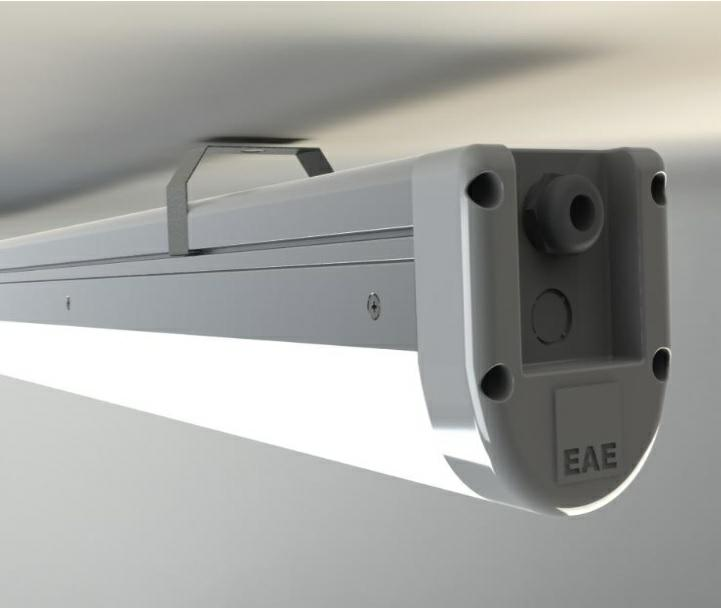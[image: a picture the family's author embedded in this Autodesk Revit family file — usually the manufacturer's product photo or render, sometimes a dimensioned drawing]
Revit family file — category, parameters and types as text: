
# Revit family: LINA
name_source: partatom
category: Lighting Fixtures
revit_build: Autodesk Revit 2016 (Build: 20150506_1715(x64)
units: mm (PartAtom-declared; Revit-internal decimal feet)

## family parameters
Cut with Voids When Loaded = No
Host = Face
Light Source = Yes
OmniClass Number = 23.80.70.11.14.17
OmniClass Title = Direct/Indirect
Part Type = Normal
Room Calculation Point = No
Round Connector Dimension = Use Diameter
Shared = No

## types (42) — shared parameters
Apparent Load = 0 VA
Assembly Code = D5020200
Ağırlık = 0.0 kg
Color Filter = 16777215
Description = SURFACE MOUNTED
Dimming Lamp Color Temperature Shift = <None>
EAE_CYi_Alum_Kasa = EAE_CYi_Alum_Kasa
EAE_CYi_Temperli Cam = EAE_CYi_Temperli Cam
Giriş Gerilimi = 220 V
IP Koruma Sınıfı = IP 65
Keynote = Catalog Number
Lamp = DO NOT USE
Lookup Table = EAE_Lookup_Annotation
Lookup Table Name = LINA
Manufacturer = EAE
Model = LINA
Photometric Web File = 1x4 2Lamp.ies
Renksel Geri Verim = CRI 80
Tilt Angle = 90.00°
Type Comments = PLEASE CONSULT EAE FOR CODE DESCRIPTION
Type Image = LINA ETANJ.jpg
URL = http://www.eaeaydinlatma.com
Wattage Comments = DO NOT USE
b = 66 mm  [stored 0.216535 ft]
h = 86 mm  [stored 0.282152 ft]
Çalışma Ortam Sıcaklığı = -25 °C / +40 °C
zero-valued in all types: Default Elevation

## per-type parameters (varying)
| type | Anma Gücü | AnnoText | Catalog Number | Emit from Line Length | Kontrol Sistem Girişi | a |
| LNE 020U 40ED00 2K0 053 | 20 W | 0 | 48407 | 512 mm  [stored 1.67979 ft] | NOT SPECIFIED | 532 mm  [stored 1.74541 ft] |
| LNE 020U 40ED01 2K0 053 | 20 W | 1 | 48408 | 512 mm  [stored 1.67979 ft] | E1h | 532 mm  [stored 1.74541 ft] |
| LNE 020U 40ED03 2K9 053 | 20 W | 3 | 48410 | 512 mm  [stored 1.67979 ft] | DALI | 532 mm  [stored 1.74541 ft] |
| LNE 020U 40ED04 2K0 053 | 20 W | 4 | 48411 | 512 mm  [stored 1.67979 ft] | DALI E1h | 532 mm  [stored 1.74541 ft] |
| LNE 020U 40ED09 2K0 063 | 20 W | 9 | 48413 | 512 mm  [stored 1.67979 ft] | SNS | 532 mm  [stored 1.74541 ft] |
| LNE 020U 40ED10 2K0 063 | 20 W | 10 | 48602 | 512 mm  [stored 1.67979 ft] | SNS E1h | 532 mm  [stored 1.74541 ft] |
| LNE 032U 40ED00 3K3 125 | 32 W | 0 | 43677 | 1230 mm  [stored 4.03543 ft] | NOT SPECIFIED | 1250 mm  [stored 4.10105 ft] |
| LNE 032U 40ED01 3K3 125 | 32 W | 1 | 43678 | 1230 mm  [stored 4.03543 ft] | E1h | 1250 mm  [stored 4.10105 ft] |
| LNE 032U 40ED02 3K3 125 | 32 W | 2 | 43679 | 1230 mm  [stored 4.03543 ft] | E3h | 1250 mm  [stored 4.10105 ft] |
| LNE 032U 40ED03 3K3 125 | 32 W | 3 | 43680 | 1230 mm  [stored 4.03543 ft] | DALI | 1250 mm  [stored 4.10105 ft] |
| LNE 032U 40ED04 3K3 125 | 32 W | 4 | 43681 | 1230 mm  [stored 4.03543 ft] | DALI E1h | 1250 mm  [stored 4.10105 ft] |
| LNE 032U 40ED05 3K3 125 | 32 W | 5 | 43682 | 1230 mm  [stored 4.03543 ft] | DALI E3h | 1250 mm  [stored 4.10105 ft] |
| LNE 032U 40ED09 3K3 135 | 32 W | 9 | 43683 | 1230 mm  [stored 4.03543 ft] | SNS | 1250 mm  [stored 4.10105 ft] |
| LNE 032U 40ED10 3K3 135 | 32 W | 10 | 48617 | 1230 mm  [stored 4.03543 ft] | SNS E1h | 1250 mm  [stored 4.10105 ft] |
| LNE 032U 40ED11 3K3 135 | 32 W | 11 | 48618 | 1230 mm  [stored 4.03543 ft] | SNS E3h | 1250 mm  [stored 4.10105 ft] |
| LNE 040U 40ED00 LLL 149 | 40 W | 0 | 48449 | 1470 mm  [stored 4.82283 ft] | NOT SPECIFIED | 1490 mm  [stored 4.88845 ft] |
| LNE 040U 40ED01 LLL 149 | 40 W | 1 | 48450 | 1470 mm  [stored 4.82283 ft] | E1h | 1490 mm  [stored 4.88845 ft] |
| LNE 040U 40ED02 LLL 149 | 40 W | 2 | 48451 | 1470 mm  [stored 4.82283 ft] | E3h | 1490 mm  [stored 4.88845 ft] |
| LNE 040U 40ED03 LLL 149 | 40 W | 3 | 48452 | 1470 mm  [stored 4.82283 ft] | DALI | 1490 mm  [stored 4.88845 ft] |
| LNE 040U 40ED04 LLL 149 | 40 W | 4 | 48453 | 1470 mm  [stored 4.82283 ft] | DALI E1h | 1490 mm  [stored 4.88845 ft] |
| LNE 040U 40ED05 LLL 149 | 40 W | 5 | 48454 | 1470 mm  [stored 4.82283 ft] | DALI E3h | 1490 mm  [stored 4.88845 ft] |
| LNE 040U 40ED09 LLL 159 | 40 W | 9 | 48455 | 1470 mm  [stored 4.82283 ft] | SNS | 1490 mm  [stored 4.88845 ft] |
| LNE 040U 40ED10 LLL 159 | 40 W | 10 | 48635 | 1470 mm  [stored 4.82283 ft] | SNS E1h | 1490 mm  [stored 4.88845 ft] |
| LNE 040U 40ED11 LLL 159 | 40 W | 11 | 48636 | 1470 mm  [stored 4.82283 ft] | SNS E3h | 1490 mm  [stored 4.88845 ft] |
| LNE 045U 40ED00 4K9 085 | 45 W | 0 | 48470 | 830 mm  [stored 2.7231 ft] | NOT SPECIFIED | 850 mm  [stored 2.78871 ft] |
| LNE 045U 40ED01 4K9 085 | 45 W | 1 | 48471 | 830 mm  [stored 2.7231 ft] | E1h | 850 mm  [stored 2.78871 ft] |
| LNE 045U 40ED02 4K9 085 | 45 W | 2 | 48472 | 830 mm  [stored 2.7231 ft] | E3h | 850 mm  [stored 2.78871 ft] |
| LNE 045U 40ED03 4K9 085 | 45 W | 3 | 48473 | 830 mm  [stored 2.7231 ft] | DALI | 850 mm  [stored 2.78871 ft] |
| LNE 045U 40ED04 4K9 085 | 45 W | 4 | 48474 | 830 mm  [stored 2.7231 ft] | DALI E1h | 850 mm  [stored 2.78871 ft] |
| LNE 045U 40ED05 4K9 085 | 45 W | 5 | 48475 | 830 mm  [stored 2.7231 ft] | DALI E3h | 850 mm  [stored 2.78871 ft] |
| LNE 045U 40ED09 4K9 095 | 45 W | 9 | 48476 | 830 mm  [stored 2.7231 ft] | SNS | 850 mm  [stored 2.78871 ft] |
| LNE 045U 40ED10 4K9 095 | 45 W | 10 | 48641 | 830 mm  [stored 2.7231 ft] | SNS E1h | 850 mm  [stored 2.78871 ft] |
| LNE 045U 40ED11 4K9 095 | 45 W | 11 | 48642 | 830 mm  [stored 2.7231 ft] | SNS E3h | 850 mm  [stored 2.78871 ft] |
| LNE 056U 40ED00 6K0 149 | 56 W | 0 | 43698 | 1470 mm  [stored 4.82283 ft] | NOT SPECIFIED | 1490 mm  [stored 4.88845 ft] |
| LNE 056U 40ED01 6K0 149 | 56 W | 1 | 43699 | 1470 mm  [stored 4.82283 ft] | E1h | 1490 mm  [stored 4.88845 ft] |
| LNE 056U 40ED02 6K0 149 | 56 W | 2 | 43700 | 1470 mm  [stored 4.82283 ft] | E3h | 1490 mm  [stored 4.88845 ft] |
| LNE 056U 40ED03 6K0 149 | 56 W | 3 | 43701 | 1470 mm  [stored 4.82283 ft] | DALI | 1490 mm  [stored 4.88845 ft] |
| LNE 056U 40ED04 6K0 149 | 56 W | 4 | 43702 | 1470 mm  [stored 4.82283 ft] | DALI E1h | 1490 mm  [stored 4.88845 ft] |
| LNE 056U 40ED05 6K0 149 | 56 W | 5 | 43703 | 1470 mm  [stored 4.82283 ft] | DALI E3h | 1490 mm  [stored 4.88845 ft] |
| LNE 056U 40ED09 6K0 159 | 56 W | 9 | 43704 | 1470 mm  [stored 4.82283 ft] | SNS | 1490 mm  [stored 4.88845 ft] |
| LNE 056U 40ED10 6K0 159 | 56 W | 10 | 48647 | 1470 mm  [stored 4.82283 ft] | SNS E1h | 1490 mm  [stored 4.88845 ft] |
| LNE 056U 40ED11 6K0 159 | 56 W | 11 | 48648 | 1470 mm  [stored 4.82283 ft] | SNS E3h | 1490 mm  [stored 4.88845 ft] |

note: column(s) folded — value = type name in every type: Ürün Kodu

note: [stored X ft] marks values corroborated as IEEE doubles in the binary element streams (Revit-internal decimal feet)

## geometry (parser evidence)
native form markers: Blend x2, Sweep x4
no freeform markers — native parametric forms only
